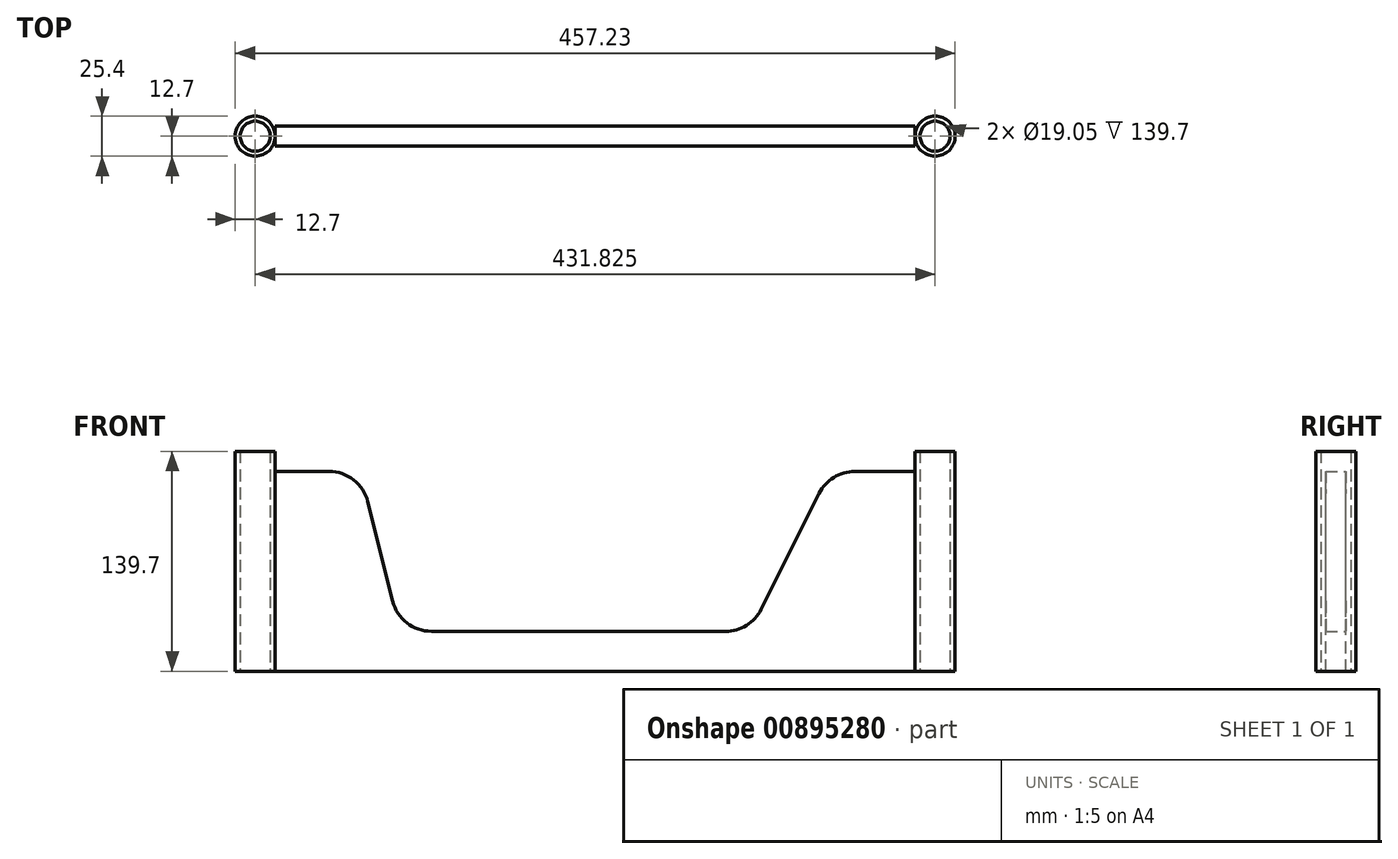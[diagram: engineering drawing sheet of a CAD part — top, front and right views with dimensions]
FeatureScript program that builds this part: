
annotation { "Feature Type Name" : "Feature", "Feature Type Description" : "" }
export const myFeature = defineFeature(function(context is Context, id is Id, definition is map)
    precondition{}
    {
        {
            var Q0;
            Q0=qCreatedBy(makeId("Front.planeOp"),FACE);
            var sketch = newSketch(context, id + "F0", { "sketchPlane" : qUnion([Q0])});
            skArc(sketch, "E0.MirrorCS", {"start": v(19.83, -297.05) * mm, "mid": v(4.2, -291.67) * mm, "end": v(-4.8, -277.81) * mm});
            skArc(sketch, "E1.MirrorCS", {"start": v(266.03, -209.5) * mm, "mid": v(275.4, -199.25) * mm, "end": v(288.75, -195.45) * mm});
            skArc(sketch, "E2.MirrorCS", {"start": v(-45.23, -195.45) * mm, "mid": v(-29.6, -200.83) * mm, "end": v(-20.6, -214.7) * mm});
            skArc(sketch, "E3.MirrorCS", {"start": v(229.27, -283.01) * mm, "mid": v(219.9, -293.26) * mm, "end": v(206.55, -297.05) * mm});
            skLineSegment(sketch, "E4.MirrorCS", {"start": v(-45.23, -195.45) * mm, "end": v(-79.38, -195.45) * mm});
            skPoint(sketch, "E5.MirrorP", {"position": v(273.05, -195.45) * mm});
            skLineSegment(sketch, "E6.MirrorCS", {"start": v(-4.8, -277.81) * mm, "end": v(-20.6, -214.7) * mm});
            skLineSegment(sketch, "E7.MirrorCS", {"start": v(19.83, -297.05) * mm, "end": v(206.55, -297.05) * mm});
            skPoint(sketch, "E8.MirrorP", {"position": v(222.25, -297.05) * mm});
            skLineSegment(sketch, "E9.MirrorCS", {"start": v(288.75, -195.45) * mm, "end": v(327.03, -195.45) * mm});
            skPoint(sketch, "E10.MirrorP", {"position": v(0, -297.05) * mm});
            skPoint(sketch, "E11.MirrorP", {"position": v(-25.4, -195.45) * mm});
            skLineSegment(sketch, "E12.MirrorCS", {"start": v(229.27, -283.01) * mm, "end": v(266.03, -209.5) * mm});
            skLineSegment(sketch, "E13.MirrorCS", {"start": v(-79.38, -322.45) * mm, "end": v(327.03, -322.45) * mm});
            skLineSegment(sketch, "E14.0", {"start": v(327.03, -322.45) * mm, "end": v(327.03, -195.45) * mm});
            skLineSegment(sketch, "E15.0", {"start": v(-79.38, -322.45) * mm, "end": v(-79.38, -195.45) * mm});
            skSolve(sketch);
        }
        {
            var Q0;
            Q0 = qSketchRegion(id + "F0", true);
            extrude(context, id + "F1", {"entities" : qUnion([Q0]), "depth" : 12.7 * mm, "offsetDistance" : 25.4 * mm});
        }
        {
            var Q0;
            Q0=makeQuery(id+"F1.opExtrude","SWEPT_FACE",FACE,{"disambiguationData":[OSD([sQuery(id+"F0.wireOp",EDGE,"E13.MirrorCS")])]});
            var sketch = newSketch(context, id + "F2", { "sketchPlane" : qUnion([Q0])});
            skCircle(sketch, "E16", {"center": v(339.73, 6.35) * mm, "radius": 12.7 * mm});
            skCircle(sketch, "E17", {"center": v(339.73, 6.35) * mm, "radius": 9.53 * mm});
            skSolve(sketch);
        }
        {
            var Q0;
            Q0 = qSketchRegion(id + "F2", true);
            extrude(context, id + "F3", {"entities" : qUnion([Q0]), "operationType" : NewBodyOperationType.ADD, "oppositeDirection" : true, "depth" : 139.7 * mm, "offsetDistance" : 25.4 * mm});
        }
        {
            var Q0;
            Q0=makeQuery(id+"F1.opExtrude","SWEPT_FACE",FACE,{"disambiguationData":[OSD([sQuery(id+"F0.wireOp",EDGE,"E13.MirrorCS")])]});
            var sketch = newSketch(context, id + "F4", { "sketchPlane" : qUnion([Q0])});
            skPoint(sketch, "E18.centerSnap0", {"position": v(-79.38, 6.35) * mm});
            skCircle(sketch, "E19", {"center": v(-92.1, 6.35) * mm, "radius": 12.7 * mm});
            skCircle(sketch, "E20", {"center": v(-92.1, 6.35) * mm, "radius": 9.53 * mm});
            skSolve(sketch);
        }
        {
            var Q0;
            Q0 = qSketchRegion(id + "F4", true);
            extrude(context, id + "F5", {"entities" : qUnion([Q0]), "oppositeDirection" : true, "depth" : 139.7 * mm, "offsetDistance" : 25.4 * mm});
        }
    });
